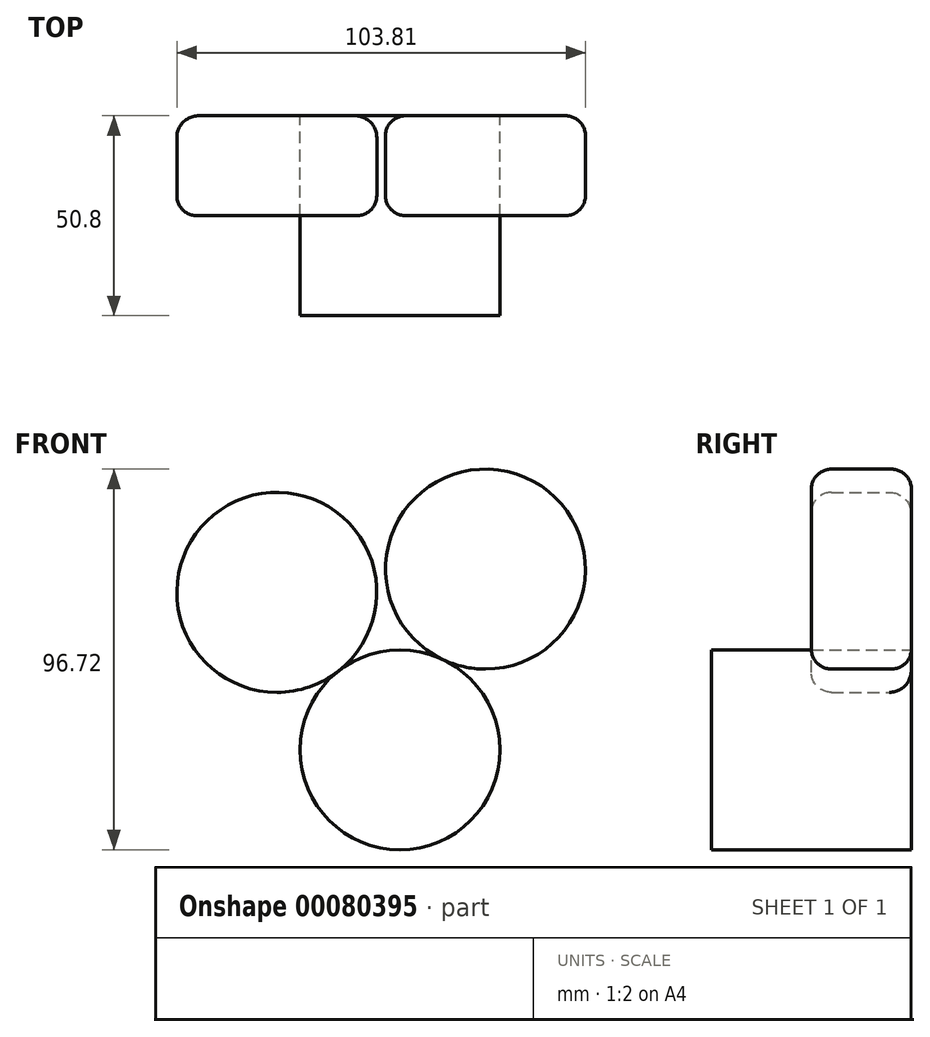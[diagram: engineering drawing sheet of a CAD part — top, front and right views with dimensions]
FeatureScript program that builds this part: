
annotation { "Feature Type Name" : "Feature", "Feature Type Description" : "" }
export const myFeature = defineFeature(function(context is Context, id is Id, definition is map)
    precondition{}
    {
        {
            var Q0;
            Q0=qCreatedBy(makeId("Front.planeOp"),FACE);
            var sketch = newSketch(context, id + "F0", { "sketchPlane" : qUnion([Q0])});
            skCircle(sketch, "E0", {"center": v(0, 0) * mm, "radius": 25.4 * mm});
            skCircle(sketch, "E1", {"center": v(-31.3, 40.02) * mm, "radius": 25.4 * mm});
            skCircle(sketch, "E2", {"center": v(21.72, 45.92) * mm, "radius": 25.4 * mm});
            skSolve(sketch);
        }
        {
            var Q0;
            Q0 = qSketchRegion(id + "F0", true);
            extrude(context, id + "F1", {"entities" : qUnion([Q0]), "depth" : 25.4 * mm});
        }
        {
            var Q0;
            Q0=makeQuery(id+"F1.opExtrude","CAP_EDGE",EDGE,{"disambiguationData":[OSD([sQuery(id+"F0.wireOp",EDGE,"E1")])],"isStart":false});
            fillet(context, id + "F2", {"entities" : qUnion([Q0]), "radius" : 5.08 * mm, "tangentPropagation" : true, "allowEdgeOverflow" : false});
        }
        {
            var Q0;
            Q0=makeQuery(id+"F1.opExtrude","SWEPT_FACE",FACE,{"disambiguationData":[OSD([sQuery(id+"F0.wireOp",EDGE,"E2")])]});
            fillet(context, id + "F3", {"entities" : qUnion([Q0]), "radius" : 5.08 * mm, "tangentPropagation" : true, "allowEdgeOverflow" : false});
        }
        {
            var Q0;
            Q0=makeQuery(id+"F1.opExtrude","CAP_FACE",FACE,{"disambiguationData":[OSD([sQuery(id+"F0.wireOp",EDGE,"E0")])],"isStart":false});
            var sketch = newSketch(context, id + "F4", { "sketchPlane" : qUnion([Q0])});
            skSolve(sketch);
        }
        {
            var Q0;
            Q0=makeQuery(id+"F1.opExtrude","CAP_FACE",FACE,{"disambiguationData":[OSD([sQuery(id+"F0.wireOp",EDGE,"E1")])],"isStart":true});
            var Q1;
            Q1=makeQuery(id+"F1.opExtrude","CAP_FACE",FACE,{"disambiguationData":[OSD([sQuery(id+"F0.wireOp",EDGE,"E1")])],"isStart":false});
            var Q2;
            Q2=makeQuery(id+"F1.opExtrude","CAP_FACE",FACE,{"disambiguationData":[OSD([sQuery(id+"F0.wireOp",EDGE,"E2")])],"isStart":false});
            fillet(context, id + "F5", {"entities" : qUnion([Q0, Q1, Q2]), "radius" : 5.6 * mm, "tangentPropagation" : true, "allowEdgeOverflow" : false});
        }
        {
            var Q0;
            Q0=makeQuery(id+"F4.imprint","IMPRINT",FACE,{"disambiguationData":[TD([[makeQuery(id+"F4.imprint","IMPRINT",EDGE,{"derivedFrom":makeQuery(id+"F1.opExtrude","CAP_EDGE",EDGE,{"disambiguationData":[OSD([sQuery(id+"F0.wireOp",EDGE,"E0")])],"isStart":false})}),1.0]])]});
            extrude(context, id + "F6", {"entities" : qUnion([Q0]), "operationType" : NewBodyOperationType.ADD, "depth" : 25.4 * mm});
        }
    });
